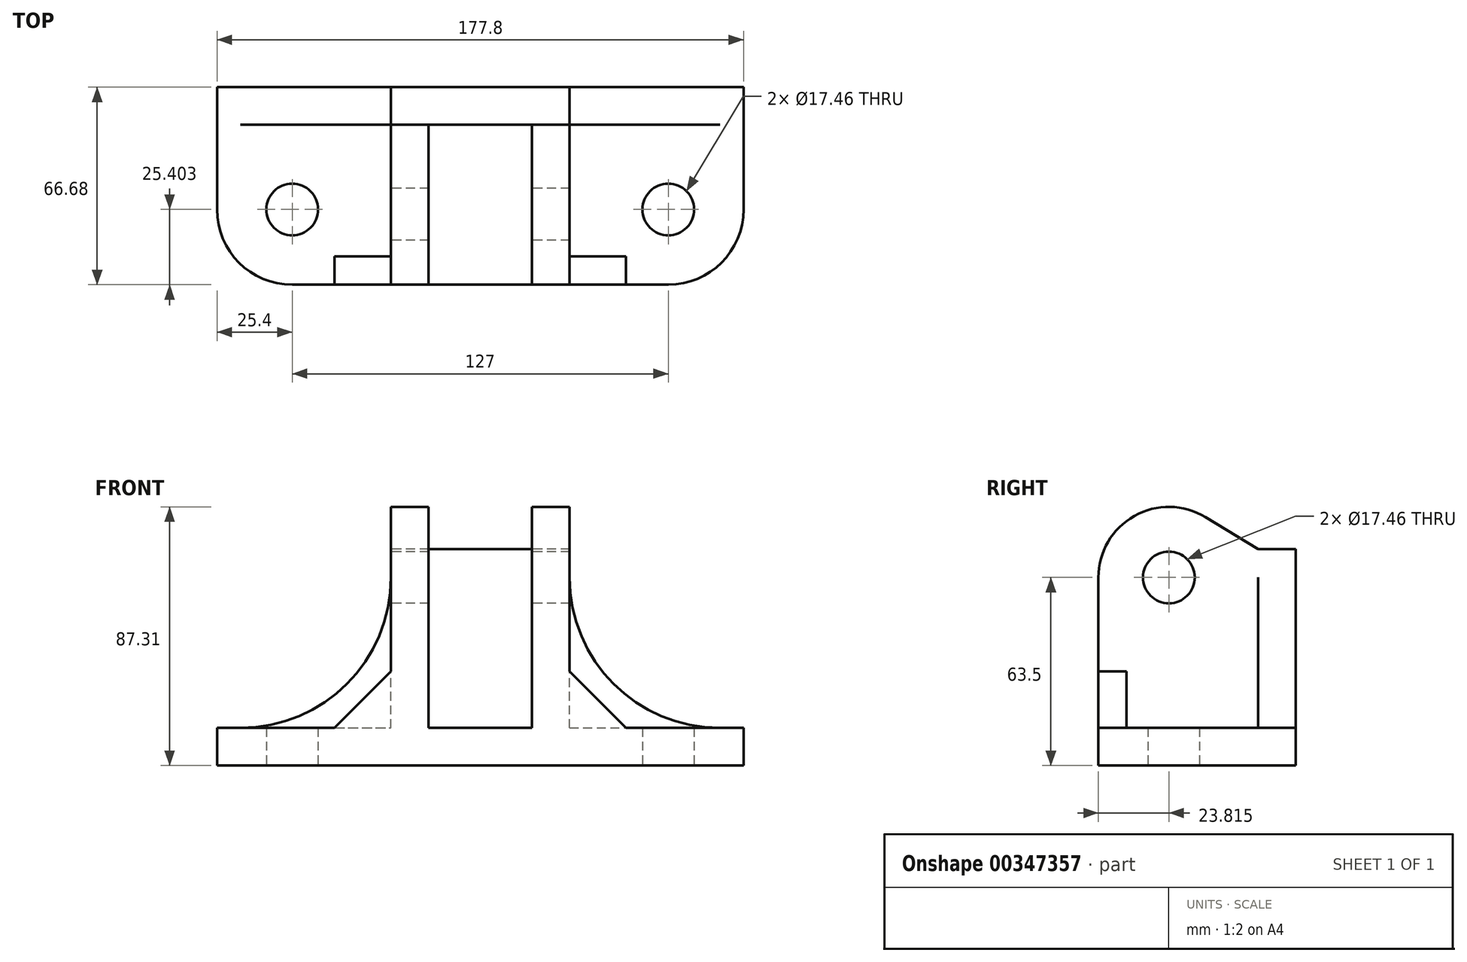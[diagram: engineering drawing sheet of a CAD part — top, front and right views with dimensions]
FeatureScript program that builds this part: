
annotation { "Feature Type Name" : "Feature", "Feature Type Description" : "" }
export const myFeature = defineFeature(function(context is Context, id is Id, definition is map)
    precondition{}
    {
        {
            var Q0;
            Q0=qCreatedBy(makeId("Top.planeOp"),FACE);
            var sketch = newSketch(context, id + "F0", { "sketchPlane" : qUnion([Q0])});
            skLineSegment(sketch, "E0.rect.bottom", {"start": v(-88.9, -33.34) * mm, "end": v(88.9, -33.34) * mm});
            skLineSegment(sketch, "E0.rect.top", {"start": v(-88.9, 33.34) * mm, "end": v(88.9, 33.34) * mm});
            skLineSegment(sketch, "E0.rect.left", {"start": v(-88.9, -33.34) * mm, "end": v(-88.9, 33.34) * mm});
            skLineSegment(sketch, "E0.rect.right", {"start": v(88.9, -33.34) * mm, "end": v(88.9, 33.34) * mm});
            skPoint(sketch, "E0.rect.middle", {"position": v(0, 0) * mm});
            skCircle(sketch, "E1", {"center": v(-63.5, -7.94) * mm, "radius": 8.73 * mm});
            skCircle(sketch, "E2", {"center": v(63.5, -7.94) * mm, "radius": 8.73 * mm});
            skLineSegment(sketch, "E3", {"start": v(0, 33.34) * mm, "end": v(0, -33.34) * mm, "construction": true});
            skCircle(sketch, "E4", {"center": v(-63.5, -7.94) * mm, "radius": 25.4 * mm});
            skCircle(sketch, "E5", {"center": v(63.5, -7.94) * mm, "radius": 25.4 * mm});
            skSolve(sketch);
        }
        {
            var Q0;
            Q0=makeQuery(id+"F0.imprint","IMPRINT",FACE,{"disambiguationData":[TD([[makeQuery(id+"F0.imprint","IMPRINT",EDGE,{"derivedFrom":sQuery(id+"F0.wireOp",EDGE,"E1")}),-1.0]])]});
            var Q1;
            {var subQ8=sQuery(id+"F0.wireOp",EDGE,"E0.rect.top");Q1=makeQuery(id+"F0.imprint","IMPRINT",FACE,{"disambiguationData":[TD([[makeQuery(id+"F0.imprint","IMPRINT",EDGE,{"derivedFrom":subQ8}),-1.0]])]});}
            var Q2;
            Q2=makeQuery(id+"F0.imprint","IMPRINT",FACE,{"disambiguationData":[TD([[makeQuery(id+"F0.imprint","IMPRINT",EDGE,{"derivedFrom":sQuery(id+"F0.wireOp",EDGE,"E2")}),-1.0]])]});
            extrude(context, id + "F1", {"entities" : qUnion([Q0, Q1, Q2]), "depth" : 12.7 * mm});
        }
        {
            var Q0;
            Q0=qCreatedBy(makeId("Right.planeOp"),FACE);
            var sketch = newSketch(context, id + "F2", { "sketchPlane" : qUnion([Q0])});
            skLineSegment(sketch, "E6.0", {"start": v(-33.34, 12.7) * mm, "end": v(-7.94, 12.7) * mm});
            skLineSegment(sketch, "E7.0", {"start": v(-7.94, 12.7) * mm, "end": v(33.34, 12.7) * mm});
            skLineSegment(sketch, "E8", {"start": v(33.34, 12.7) * mm, "end": v(33.34, 73.03) * mm});
            skLineSegment(sketch, "E9", {"start": v(33.34, 73.03) * mm, "end": v(20.64, 73.03) * mm});
            skLineSegment(sketch, "E10", {"start": v(-33.34, 12.7) * mm, "end": v(-33.34, 63.5) * mm});
            skCircle(sketch, "E11", {"center": v(-9.52, 63.5) * mm, "radius": 23.81 * mm});
            skCircle(sketch, "E12", {"center": v(-9.52, 63.5) * mm, "radius": 8.73 * mm});
            skLineSegment(sketch, "E13", {"start": v(20.64, 73.03) * mm, "end": v(0, 85.58) * mm});
            skSolve(sketch);
        }
        {
            var Q0;
            Q0=makeQuery(id+"F2.imprint","IMPRINT",FACE,{"disambiguationData":[TD([[makeQuery(id+"F2.imprint","IMPRINT",EDGE,{"derivedFrom":sQuery(id+"F2.wireOp",EDGE,"E6.0")}),1.0]])]});
            var Q1;
            Q1=makeQuery(id+"F2.imprint","IMPRINT",FACE,{"disambiguationData":[TD([[makeQuery(id+"F2.imprint","IMPRINT",EDGE,{"derivedFrom":sQuery(id+"F2.wireOp",EDGE,"E12")}),-1.0]])]});
            extrude(context, id + "F3", {"entities" : qUnion([Q0, Q1]), "operationType" : NewBodyOperationType.ADD, "depth" : 60.32 * mm, "symmetric" : true});
        }
        {
            var Q0;
            Q0=qCreatedBy(makeId("Right.planeOp"),FACE);
            var sketch = newSketch(context, id + "F4", { "sketchPlane" : qUnion([Q0])});
            skLineSegment(sketch, "E14.0", {"start": v(33.34, 73.03) * mm, "end": v(20.64, 73.03) * mm});
            skLineSegment(sketch, "E15.0", {"start": v(-7.94, 12.7) * mm, "end": v(33.34, 12.7) * mm});
            skLineSegment(sketch, "E16", {"start": v(20.64, 73.03) * mm, "end": v(20.64, 12.7) * mm});
            skArc(sketch, "E17.0", {"start": v(2.85, 83.84) * mm, "mid": v(-21.2, 84.26) * mm, "end": v(-33.34, 63.5) * mm});
            skLineSegment(sketch, "E18.0", {"start": v(20.64, 73.03) * mm, "end": v(2.85, 83.84) * mm});
            skLineSegment(sketch, "E19.0", {"start": v(-33.34, 12.7) * mm, "end": v(-33.34, 63.5) * mm});
            skLineSegment(sketch, "E20.0", {"start": v(-33.34, 12.7) * mm, "end": v(-7.94, 12.7) * mm});
            skSolve(sketch);
        }
        {
            var Q0;
            Q0=qSketchRegion(id+"F4",true);
            extrude(context, id + "F5", {"entities" : qUnion([Q0]), "operationType" : NewBodyOperationType.REMOVE, "oppositeDirection" : true, "depth" : 34.92 * mm, "symmetric" : true});
        }
        {
            var Q0;
            Q0=makeQuery(id+"F3.boolean.opBoolean","MERGE",FACE,{"derivedFrom":[makeQuery(id+"F1.opExtrude","SWEPT_FACE",FACE,{"disambiguationData":[OSD([sQuery(id+"F0.wireOp",EDGE,"E0.rect.bottom")])]}),makeQuery(id+"F3.opExtrude","SWEPT_FACE",FACE,{"disambiguationData":[OSD([sQuery(id+"F2.wireOp",EDGE,"E10")])]})]});
            var sketch = newSketch(context, id + "F6", { "sketchPlane" : qUnion([Q0])});
            skLineSegment(sketch, "E21.0", {"start": v(30.16, 12.7) * mm, "end": v(30.16, 63.5) * mm});
            skLineSegment(sketch, "E22.0", {"start": v(30.16, 12.7) * mm, "end": v(63.5, 12.7) * mm});
            skLineSegment(sketch, "E23.0", {"start": v(-30.16, 12.7) * mm, "end": v(-30.16, 63.5) * mm});
            skLineSegment(sketch, "E24.0", {"start": v(-63.5, 12.7) * mm, "end": v(-30.16, 12.7) * mm});
            skLineSegment(sketch, "E25", {"start": v(30.16, 31.75) * mm, "end": v(49.21, 12.7) * mm});
            skLineSegment(sketch, "E26", {"start": v(-30.16, 31.75) * mm, "end": v(-49.21, 12.7) * mm});
            skSolve(sketch);
        }
        {
            var Q0;
            {var subQ0=sQuery(id+"F6.wireOp",EDGE,"E26");Q0=makeQuery(id+"F6.imprint","IMPRINT",FACE,{"disambiguationData":[TD([[makeQuery(id+"F6.imprint","IMPRINT",EDGE,{"derivedFrom":subQ0}),1.0]])]});}
            var Q1;
            {var subQ0=sQuery(id+"F6.wireOp",EDGE,"E25");Q1=makeQuery(id+"F6.imprint","IMPRINT",FACE,{"disambiguationData":[TD([[makeQuery(id+"F6.imprint","IMPRINT",EDGE,{"derivedFrom":subQ0}),-1.0]])]});}
            extrude(context, id + "F7", {"entities" : qUnion([Q0, Q1]), "operationType" : NewBodyOperationType.ADD, "oppositeDirection" : true, "depth" : 9.52 * mm});
        }
        {
            var Q0;
            Q0=makeQuery(id+"F3.boolean.opBoolean","MERGE",FACE,{"derivedFrom":[makeQuery(id+"F1.opExtrude","SWEPT_FACE",FACE,{"disambiguationData":[OSD([sQuery(id+"F0.wireOp",EDGE,"E0.rect.top")])]}),makeQuery(id+"F3.opExtrude","SWEPT_FACE",FACE,{"disambiguationData":[OSD([sQuery(id+"F2.wireOp",EDGE,"E8")])]})]});
            var sketch = newSketch(context, id + "F8", { "sketchPlane" : qUnion([Q0])});
            skLineSegment(sketch, "E27.0", {"start": v(-80.96, 12.7) * mm, "end": v(-88.9, 12.7) * mm});
            skLineSegment(sketch, "E28.0", {"start": v(-30.16, 63.5) * mm, "end": v(-30.16, 73.03) * mm});
            skLineSegment(sketch, "E29.0", {"start": v(30.16, 63.5) * mm, "end": v(30.16, 73.03) * mm});
            skLineSegment(sketch, "E30.0", {"start": v(88.9, 12.7) * mm, "end": v(80.96, 12.7) * mm});
            skPoint(sketch, "E31.visualSharp", {"position": v(-30.16, 12.7) * mm});
            skArc(sketch, "E31.filletArc", {"start": v(-80.96, 12.7) * mm, "mid": v(-45.04, 27.58) * mm, "end": v(-30.16, 63.5) * mm});
            skPoint(sketch, "E32.visualSharp", {"position": v(30.16, 12.7) * mm});
            skArc(sketch, "E32.filletArc", {"start": v(30.16, 63.5) * mm, "mid": v(45.04, 27.58) * mm, "end": v(80.96, 12.7) * mm});
            skSolve(sketch);
        }
        {
            var Q0;
            {var subQ4=sQuery(id+"F8.wireOp",EDGE,"E31.filletArc");Q0=makeQuery(id+"F8.imprint","IMPRINT",FACE,{"disambiguationData":[TD([[makeQuery(id+"F8.imprint","IMPRINT",EDGE,{"derivedFrom":subQ4}),-1.0]])]});}
            var Q1;
            {var subQ4=sQuery(id+"F8.wireOp",EDGE,"E32.filletArc");Q1=makeQuery(id+"F8.imprint","IMPRINT",FACE,{"disambiguationData":[TD([[makeQuery(id+"F8.imprint","IMPRINT",EDGE,{"derivedFrom":subQ4}),-1.0]])]});}
            var Q2;
            Q2=makeQuery(id+"F5.boolean.opBoolean","COPY",FACE,{"derivedFrom":makeQuery(id+"F5.opExtrude","SWEPT_FACE",FACE,{"disambiguationData":[OSD([sQuery(id+"F4.wireOp",EDGE,"E16")])]})});
            extrude(context, id + "F9", {"entities" : qUnion([Q0, Q1]), "operationType" : NewBodyOperationType.ADD, "endBound" : BoundingType.UP_TO_SURFACE, "oppositeDirection" : true, "endBoundEntityFace" : qUnion([Q2]), "depth" : 25.4 * mm});
        }
    });
